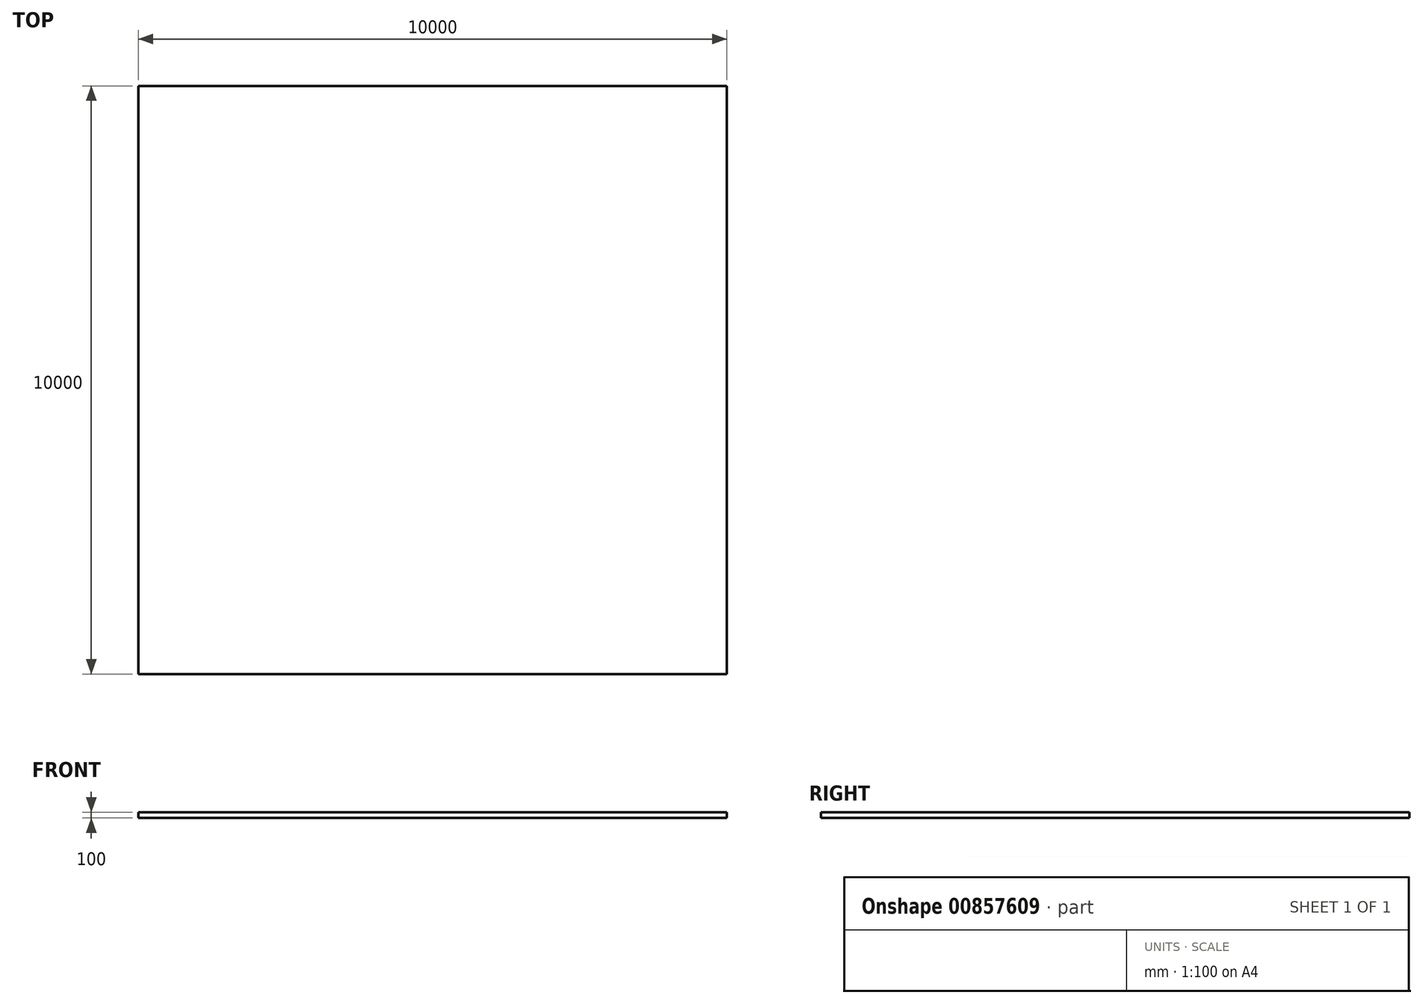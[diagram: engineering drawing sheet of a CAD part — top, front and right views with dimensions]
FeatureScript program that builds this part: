
annotation { "Feature Type Name" : "Feature", "Feature Type Description" : "" }
export const myFeature = defineFeature(function(context is Context, id is Id, definition is map)
    precondition{}
    {
        {
            var Q0;
            Q0=qCreatedBy(makeId("Top.planeOp"),FACE);
            var sketch = newSketch(context, id + "F0", { "sketchPlane" : qUnion([Q0])});
            skLineSegment(sketch, "E0.bottom", {"start": v(5000, 5000) * mm, "end": v(-5000, 5000) * mm});
            skLineSegment(sketch, "E0.top", {"start": v(5000, -5000) * mm, "end": v(-5000, -5000) * mm});
            skLineSegment(sketch, "E0.left", {"start": v(5000, 5000) * mm, "end": v(5000, -5000) * mm});
            skLineSegment(sketch, "E0.right", {"start": v(-5000, 5000) * mm, "end": v(-5000, -5000) * mm});
            skPoint(sketch, "E0.middle", {"position": v(0, 0) * mm});
            skSolve(sketch);
        }
        {
            var Q0;
            Q0 = qSketchRegion(id + "F0", true);
            extrude(context, id + "F1", {"entities" : qUnion([Q0]), "depth" : 100 * mm, "offsetDistance" : 25.4 * mm});
        }
    });
